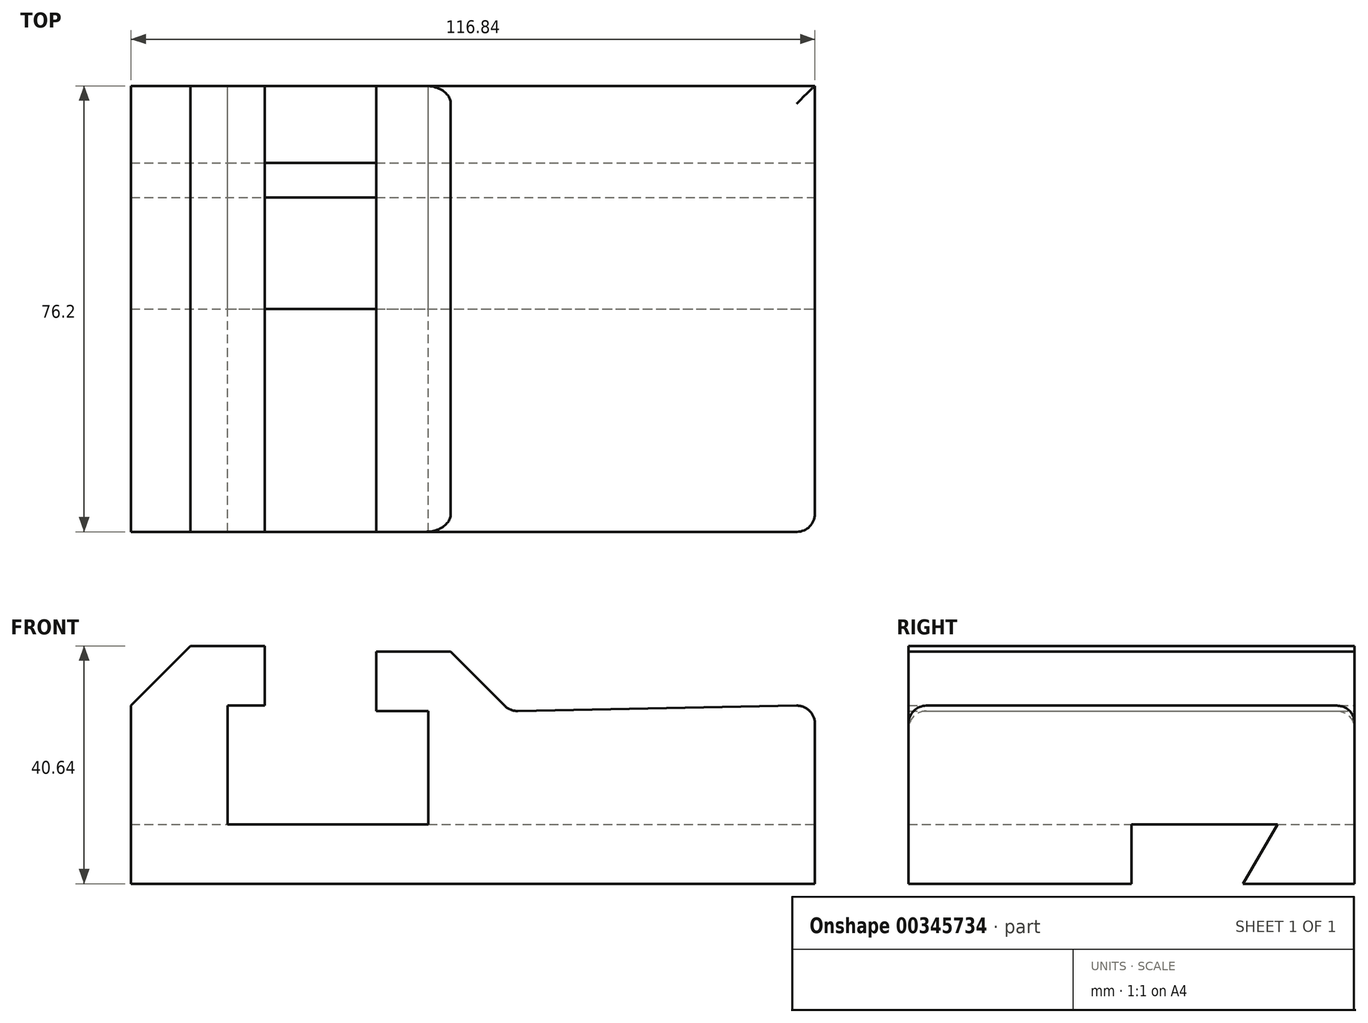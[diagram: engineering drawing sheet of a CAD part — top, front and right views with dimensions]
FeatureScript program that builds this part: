
annotation { "Feature Type Name" : "Feature", "Feature Type Description" : "" }
export const myFeature = defineFeature(function(context is Context, id is Id, definition is map)
    precondition{}
    {
        {
            var Q0;
            Q0=qCreatedBy(makeId("Front.planeOp"),FACE);
            var sketch = newSketch(context, id + "F0", { "sketchPlane" : qUnion([Q0])});
            skLineSegment(sketch, "E0", {"start": v(62.54, -21.5) * mm, "end": v(-54.3, -21.5) * mm});
            skLineSegment(sketch, "E1", {"start": v(-54.3, -21.5) * mm, "end": v(-54.3, 19.14) * mm});
            skLineSegment(sketch, "E2", {"start": v(-54.3, 19.14) * mm, "end": v(-31.44, 19.14) * mm});
            skLineSegment(sketch, "E3", {"start": v(-31.44, 19.14) * mm, "end": v(-31.44, 8.98) * mm});
            skLineSegment(sketch, "E4", {"start": v(-31.44, 8.98) * mm, "end": v(-37.8, 8.98) * mm});
            skLineSegment(sketch, "E5", {"start": v(-37.8, -11.34) * mm, "end": v(-37.8, 8.98) * mm});
            skLineSegment(sketch, "E6", {"start": v(-37.8, -11.34) * mm, "end": v(-3.5, -11.34) * mm});
            skLineSegment(sketch, "E7", {"start": v(-3.5, -11.34) * mm, "end": v(-3.5, 7.98) * mm});
            skLineSegment(sketch, "E8", {"start": v(-3.5, 7.98) * mm, "end": v(-12.4, 7.98) * mm});
            skLineSegment(sketch, "E9", {"start": v(-12.4, 7.98) * mm, "end": v(-12.4, 18.14) * mm});
            skLineSegment(sketch, "E10", {"start": v(-12.4, 18.14) * mm, "end": v(0.3, 18.14) * mm});
            skLineSegment(sketch, "E11", {"start": v(0.3, 18.14) * mm, "end": v(0.3, 7.98) * mm});
            skLineSegment(sketch, "E12", {"start": v(62.54, -21.5) * mm, "end": v(62.54, 8.98) * mm});
            skLineSegment(sketch, "E13", {"start": v(0.3, 7.98) * mm, "end": v(10.47, 7.98) * mm});
            skLineSegment(sketch, "E14", {"start": v(0.3, 18.14) * mm, "end": v(10.47, 7.98) * mm});
            skLineSegment(sketch, "E15", {"start": v(62.54, 8.98) * mm, "end": v(10.47, 7.98) * mm});
            skLineSegment(sketch, "E16", {"start": v(-54.3, 8.98) * mm, "end": v(-44.14, 19.14) * mm});
            skSolve(sketch);
        }
        {
            var Q0;
            Q0=makeQuery(id+"F0.imprint","IMPRINT",FACE,{"disambiguationData":[TD([[makeQuery(id+"F0.imprint","IMPRINT",EDGE,{"derivedFrom":sQuery(id+"F0.wireOp",EDGE,"E11")}),1.0]])]});
            var Q1;
            {var subQ0=sQuery(id+"F0.wireOp",EDGE,"E0");Q1=makeQuery(id+"F0.imprint","IMPRINT",FACE,{"disambiguationData":[TD([[makeQuery(id+"F0.imprint","IMPRINT",EDGE,{"derivedFrom":subQ0}),-1.0]])]});}
            extrude(context, id + "F1", {"entities" : qUnion([Q0, Q1]), "endBound" : BoundingType.SYMMETRIC, "depth" : 76.2 * mm});
        }
        {
            var Q0;
            Q0=makeQuery(id+"F1.opExtrude","CAP_EDGE",EDGE,{"disambiguationData":[OSD([sQuery(id+"F0.wireOp",EDGE,"E14")])],"isStart":false});
            var Q1;
            Q1=makeQuery(id+"F1.opExtrude","CAP_EDGE",EDGE,{"disambiguationData":[OSD([sQuery(id+"F0.wireOp",EDGE,"E15")])],"isStart":false});
            var Q2;
            Q2=makeQuery(id+"F1.opExtrude","CAP_EDGE",EDGE,{"disambiguationData":[OSD([sQuery(id+"F0.wireOp",EDGE,"E12")])],"isStart":false});
            var Q3;
            Q3=makeQuery(id+"F1.opExtrude","SWEPT_EDGE",EDGE,{"disambiguationData":[OSD([sQuery(id+"F0.wireOp",EDGE,"E12"),sQuery(id+"F0.wireOp",EDGE,"E15")])]});
            var Q4;
            Q4=makeQuery(id+"F1.opExtrude","SWEPT_EDGE",EDGE,{"disambiguationData":[OSD([sQuery(id+"F0.wireOp",EDGE,"E13"),sQuery(id+"F0.wireOp",EDGE,"E14"),sQuery(id+"F0.wireOp",EDGE,"E15")])]});
            var Q5;
            Q5=makeQuery(id+"F1.opExtrude","CAP_EDGE",EDGE,{"disambiguationData":[OSD([sQuery(id+"F0.wireOp",EDGE,"E15")])],"isStart":true});
            var Q6;
            Q6=makeQuery(id+"F1.opExtrude","CAP_EDGE",EDGE,{"disambiguationData":[OSD([sQuery(id+"F0.wireOp",EDGE,"E14")])],"isStart":true});
            fillet(context, id + "F2", {"entities" : qUnion([Q0, Q1, Q2, Q3, Q4, Q5, Q6]), "radius" : 3.05 * mm, "tangentPropagation" : true, "allowEdgeOverflow" : false});
        }
        {
            var Q0;
            Q0=makeQuery(id+"F1.opExtrude","SWEPT_FACE",FACE,{"disambiguationData":[OSD([sQuery(id+"F0.wireOp",EDGE,"E12")])]});
            var sketch = newSketch(context, id + "F3", { "sketchPlane" : qUnion([Q0])});
            skLineSegment(sketch, "E17", {"start": v(0, -21.5) * mm, "end": v(-19.05, -21.5) * mm});
            skLineSegment(sketch, "E18", {"start": v(-19.05, -21.5) * mm, "end": v(0, -21.5) * mm});
            skLineSegment(sketch, "E19", {"start": v(19.05, -21.5) * mm, "end": v(0, -21.5) * mm});
            skLineSegment(sketch, "E20", {"start": v(-19.05, -21.5) * mm, "end": v(-21.8, -16.72) * mm});
            skLineSegment(sketch, "E21", {"start": v(0, -21.5) * mm, "end": v(0, -11.34) * mm});
            skLineSegment(sketch, "E22", {"start": v(0, -11.34) * mm, "end": v(-25.16, -11.34) * mm});
            skLineSegment(sketch, "E23", {"start": v(19.05, -21.5) * mm, "end": v(24.92, -11.34) * mm});
            skLineSegment(sketch, "E24", {"start": v(24.92, -11.34) * mm, "end": v(0, -11.34) * mm});
            skLineSegment(sketch, "E25", {"start": v(-21.8, -16.72) * mm, "end": v(-25.16, -11.34) * mm});
            skSolve(sketch);
        }
        {
            var Q0;
            Q0=makeQuery(id+"F3.imprint","IMPRINT",FACE,{"disambiguationData":[TD([[makeQuery(id+"F3.imprint","IMPRINT",EDGE,{"derivedFrom":sQuery(id+"F3.wireOp",EDGE,"E19")}),1.0]])]});
            var Q1;
            Q1=makeQuery(id+"F3.imprint","IMPRINT",FACE,{"disambiguationData":[TD([[makeQuery(id+"F3.imprint","IMPRINT",EDGE,{"derivedFrom":sQuery(id+"F3.wireOp",EDGE,"E18")}),1.0]])]});
            extrude(context, id + "F4", {"entities" : qUnion([Q0, Q1]), "operationType" : NewBodyOperationType.REMOVE, "oppositeDirection" : true, "depth" : 116.84 * mm});
        }
    });
